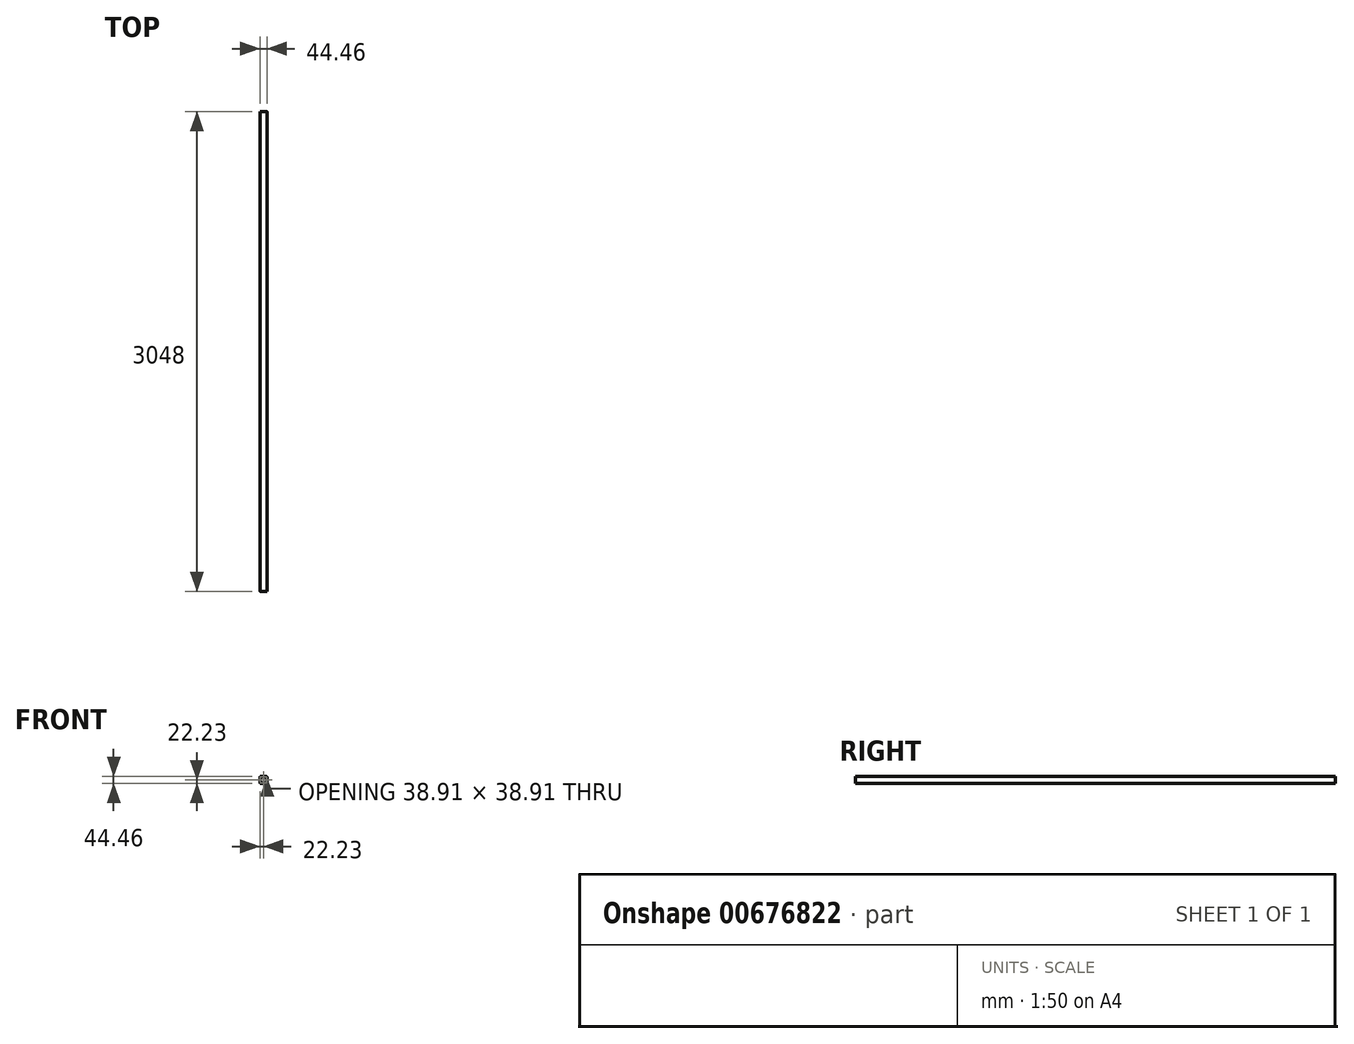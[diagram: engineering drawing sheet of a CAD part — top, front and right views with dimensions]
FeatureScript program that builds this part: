
annotation { "Feature Type Name" : "Feature", "Feature Type Description" : "" }
export const myFeature = defineFeature(function(context is Context, id is Id, definition is map)
    precondition{}
    {
        {
            var Q0;
            Q0=qCreatedBy(makeId("Front.planeOp"),FACE);
            var sketch = newSketch(context, id + "F0", { "sketchPlane" : qUnion([Q0])});
            skLineSegment(sketch, "E0.bottom", {"start": v(15.87, -22.22) * mm, "end": v(-15.87, -22.23) * mm});
            skLineSegment(sketch, "E0.top", {"start": v(15.88, 22.23) * mm, "end": v(-15.88, 22.22) * mm});
            skLineSegment(sketch, "E0.left", {"start": v(22.23, -15.87) * mm, "end": v(22.23, 15.88) * mm});
            skLineSegment(sketch, "E0.right", {"start": v(-22.23, -15.88) * mm, "end": v(-22.23, 15.87) * mm});
            skPoint(sketch, "E0.middle", {"position": v(0, 0) * mm});
            skPoint(sketch, "E1.visualSharp", {"position": v(-22.23, 22.22) * mm});
            skArc(sketch, "E1.filletArc", {"start": v(-15.88, 22.22) * mm, "mid": v(-20.37, 20.37) * mm, "end": v(-22.23, 15.87) * mm});
            skPoint(sketch, "E2.visualSharp", {"position": v(22.23, 22.23) * mm});
            skArc(sketch, "E2.filletArc", {"start": v(22.23, 15.88) * mm, "mid": v(20.37, 20.37) * mm, "end": v(15.88, 22.23) * mm});
            skPoint(sketch, "E3.visualSharp", {"position": v(22.23, -22.22) * mm});
            skArc(sketch, "E3.filletArc", {"start": v(15.87, -22.22) * mm, "mid": v(20.37, -20.37) * mm, "end": v(22.23, -15.87) * mm});
            skPoint(sketch, "E4.visualSharp", {"position": v(-22.23, -22.23) * mm});
            skArc(sketch, "E4.filletArc", {"start": v(-22.23, -15.88) * mm, "mid": v(-20.37, -20.37) * mm, "end": v(-15.87, -22.23) * mm});
            skSolve(sketch);
        }
        {
            var Q0;
            Q0=makeQuery(id+"F0.imprint","IMPRINT",FACE,{"disambiguationData":[TD([[makeQuery(id+"F0.imprint","IMPRINT",EDGE,{"derivedFrom":sQuery(id+"F0.wireOp",EDGE,"E0.bottom")}),-1.0]])]});
            extrude(context, id + "F1", {"entities" : qUnion([Q0]), "oppositeDirection" : true, "depth" : 1524 * mm, "offsetDistance" : 25.4 * mm, "hasSecondDirection" : true, "secondDirectionOppositeDirection" : false, "secondDirectionDepth" : 1524 * mm});
        }
        {
            var Q0;
            Q0=makeQuery(id+"F1.opExtrude","CAP_FACE",FACE,{"disambiguationData":[OSD([sQuery(id+"F0.wireOp",EDGE,"E0.bottom"),sQuery(id+"F0.wireOp",EDGE,"E0.top"),sQuery(id+"F0.wireOp",EDGE,"E0.left"),sQuery(id+"F0.wireOp",EDGE,"E0.right"),sQuery(id+"F0.wireOp",EDGE,"E1.filletArc"),sQuery(id+"F0.wireOp",EDGE,"E2.filletArc"),sQuery(id+"F0.wireOp",EDGE,"E3.filletArc"),sQuery(id+"F0.wireOp",EDGE,"E4.filletArc")])],"isStart":true});
            var sketch = newSketch(context, id + "F2", { "sketchPlane" : qUnion([Q0])});
            skLineSegment(sketch, "E5.bottom", {"start": v(16.28, -19.46) * mm, "end": v(-16.28, -19.46) * mm});
            skLineSegment(sketch, "E5.top", {"start": v(16.28, 19.46) * mm, "end": v(-16.28, 19.46) * mm});
            skLineSegment(sketch, "E5.left", {"start": v(19.46, -16.28) * mm, "end": v(19.46, 16.28) * mm});
            skLineSegment(sketch, "E5.right", {"start": v(-19.46, -16.28) * mm, "end": v(-19.46, 16.28) * mm});
            skPoint(sketch, "E5.middle", {"position": v(0, 0) * mm});
            skPoint(sketch, "E6.visualSharp", {"position": v(-19.46, 19.46) * mm});
            skArc(sketch, "E6.filletArc", {"start": v(-16.28, 19.46) * mm, "mid": v(-18.53, 18.53) * mm, "end": v(-19.46, 16.28) * mm});
            skPoint(sketch, "E7.visualSharp", {"position": v(19.46, 19.46) * mm});
            skArc(sketch, "E7.filletArc", {"start": v(19.46, 16.28) * mm, "mid": v(18.53, 18.53) * mm, "end": v(16.28, 19.46) * mm});
            skPoint(sketch, "E8.visualSharp", {"position": v(19.46, -19.46) * mm});
            skArc(sketch, "E8.filletArc", {"start": v(16.28, -19.46) * mm, "mid": v(18.53, -18.53) * mm, "end": v(19.46, -16.28) * mm});
            skPoint(sketch, "E9.visualSharp", {"position": v(-19.46, -19.46) * mm});
            skArc(sketch, "E9.filletArc", {"start": v(-19.46, -16.28) * mm, "mid": v(-18.53, -18.53) * mm, "end": v(-16.28, -19.46) * mm});
            skSolve(sketch);
        }
        {
            var Q0;
            Q0=makeQuery(id+"F2.imprint","IMPRINT",FACE,{"disambiguationData":[TD([[makeQuery(id+"F2.imprint","IMPRINT",EDGE,{"derivedFrom":sQuery(id+"F2.wireOp",EDGE,"E5.bottom")}),-1.0]])]});
            extrude(context, id + "F3", {"entities" : qUnion([Q0]), "operationType" : NewBodyOperationType.REMOVE, "endBound" : BoundingType.THROUGH_ALL, "oppositeDirection" : true, "depth" : 25.4 * mm, "offsetDistance" : 25.4 * mm});
        }
    });
